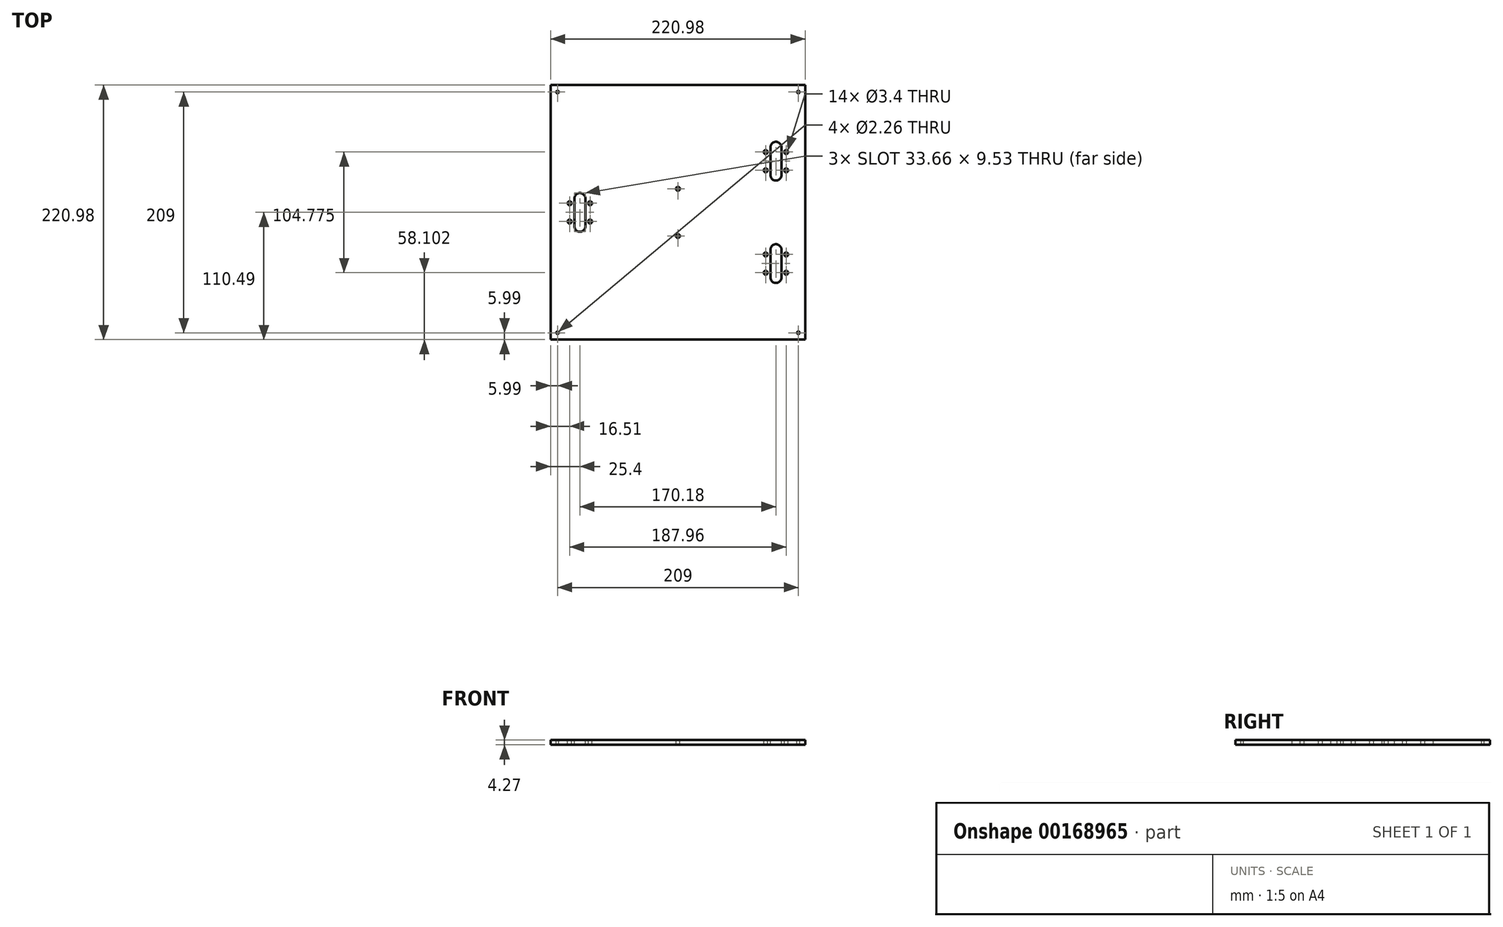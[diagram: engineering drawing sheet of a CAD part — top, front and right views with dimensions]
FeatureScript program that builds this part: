
annotation { "Feature Type Name" : "Feature", "Feature Type Description" : "" }
export const myFeature = defineFeature(function(context is Context, id is Id, definition is map)
    precondition{}
    {
        {
            var Q0;
            Q0=qCreatedBy(makeId("Top.planeOp"),FACE);
            var sketch = newSketch(context, id + "F0", { "sketchPlane" : qUnion([Q0])});
            skLineSegment(sketch, "E0.bottom", {"start": v(0, 0) * mm, "end": v(220.98, 0) * mm});
            skLineSegment(sketch, "E0.top", {"start": v(0, 220.98) * mm, "end": v(220.98, 220.98) * mm});
            skLineSegment(sketch, "E0.left", {"start": v(0, 0) * mm, "end": v(0, 220.98) * mm});
            skLineSegment(sketch, "E0.right", {"start": v(220.98, 0) * mm, "end": v(220.98, 220.98) * mm});
            skSolve(sketch);
        }
        {
            var Q0;
            Q0=makeQuery(id+"F0.imprint","IMPRINT",FACE,{"disambiguationData":[TD([[makeQuery(id+"F0.imprint","IMPRINT",EDGE,{"derivedFrom":sQuery(id+"F0.wireOp",EDGE,"E0.bottom")}),1.0]])]});
            extrude(context, id + "F1", {"entities" : qUnion([Q0]), "depth" : 4.27 * mm});
        }
        {
            var Q0;
            Q0=makeQuery(id+"F1.opExtrude","CAP_FACE",FACE,{"disambiguationData":[OSD([sQuery(id+"F0.wireOp",EDGE,"E0.bottom"),sQuery(id+"F0.wireOp",EDGE,"E0.top"),sQuery(id+"F0.wireOp",EDGE,"E0.left"),sQuery(id+"F0.wireOp",EDGE,"E0.right")])],"isStart":false});
            var sketch = newSketch(context, id + "F2", { "sketchPlane" : qUnion([Q0])});
            skLineSegment(sketch, "E1", {"start": v(110.5, 0) * mm, "end": v(110.5, 220.98) * mm});
            skLineSegment(sketch, "E2", {"start": v(0, 110.5) * mm, "end": v(220.98, 110.5) * mm});
            skPoint(sketch, "E3", {"position": v(6, 215) * mm});
            skPoint(sketch, "E4.MirrorP", {"position": v(214.99, 215) * mm});
            skPoint(sketch, "E5.MirrorP", {"position": v(215, 6) * mm});
            skPoint(sketch, "E6.MirrorP", {"position": v(6, 6) * mm});
            skSolve(sketch);
        }
        {
            var Q0;
            Q0=sQuery(id+"F2.wireOp",VERTEX,"E3");
            var Q1;
            Q1=sQuery(id+"F2.wireOp",VERTEX,"E4.MirrorP");
            var Q2;
            Q2=sQuery(id+"F2.wireOp",VERTEX,"E5.MirrorP");
            var Q3;
            Q3=sQuery(id+"F2.wireOp",VERTEX,"E6.MirrorP");
            var Q4;
            Q4=makeQuery(id+"F1.opExtrude","SWEPT_BODY",BODY,{"disambiguationData":[OSD([sQuery(id+"F0.wireOp",EDGE,"E0.bottom"),sQuery(id+"F0.wireOp",EDGE,"E0.top"),sQuery(id+"F0.wireOp",EDGE,"E0.left"),sQuery(id+"F0.wireOp",EDGE,"E0.right")])]});
            hole(context, id + "F3", {"style" : HoleStyle.SIMPLE, "endStyle" : HoleEndStyle.THROUGH, "standardTappedOrClearance" : lookupTablePath({ "standard" : "ANSI", "engagement" : "75%", "pitch" : "40 tpi", "size" : "#4", "type" : "Tapped" }), "standardBlindInLast" : lookupTablePath({ "standard" : "ANSI", "engagement" : "75%", "pitch" : "40 tpi", "size" : "#4", "type" : "Tapped" }), "holeDiameter" : 2.26 * mm, "locations" : qUnion([Q0, Q1, Q2, Q3]), "scope" : qUnion([Q4]), "isTappedThrough" : true, "majorDiameter" : 2.84 * mm, "showTappedDepth" : true});
        }
        {
            var Q0;
            Q0=makeQuery(id+"F1.opExtrude","CAP_FACE",FACE,{"disambiguationData":[OSD([sQuery(id+"F0.wireOp",EDGE,"E0.bottom"),sQuery(id+"F0.wireOp",EDGE,"E0.top"),sQuery(id+"F0.wireOp",EDGE,"E0.left"),sQuery(id+"F0.wireOp",EDGE,"E0.right")])],"isStart":false});
            var sketch = newSketch(context, id + "F4", { "sketchPlane" : qUnion([Q0])});
            skLineSegment(sketch, "E7", {"start": v(110.5, 220.98) * mm, "end": v(110.5, 0) * mm, "construction": true});
            skLineSegment(sketch, "E8", {"start": v(25.4, 220.98) * mm, "end": v(25.4, 0) * mm, "construction": true});
            skLineSegment(sketch, "E9.MirrorCS", {"start": v(195.58, 220.98) * mm, "end": v(195.58, 0) * mm, "construction": true});
            skLineSegment(sketch, "E10", {"start": v(0, 110.5) * mm, "end": v(220.98, 110.5) * mm, "construction": true});
            skLineSegment(sketch, "E11.left", {"start": v(20.64, 122.55) * mm, "end": v(20.64, 98.42) * mm});
            skLineSegment(sketch, "E11.right", {"start": v(30.16, 122.55) * mm, "end": v(30.16, 98.42) * mm});
            skArc(sketch, "E12", {"start": v(20.64, 122.55) * mm, "mid": v(25.4, 127.32) * mm, "end": v(30.16, 122.55) * mm});
            skArc(sketch, "E13.MirrorCS", {"start": v(20.64, 98.42) * mm, "mid": v(25.4, 93.66) * mm, "end": v(30.16, 98.42) * mm});
            skLineSegment(sketch, "E14.left", {"start": v(190.82, 78.1) * mm, "end": v(190.82, 53.98) * mm});
            skLineSegment(sketch, "E14.right", {"start": v(200.34, 78.1) * mm, "end": v(200.34, 53.98) * mm});
            skPoint(sketch, "E14.middle", {"position": v(195.58, 66.04) * mm});
            skArc(sketch, "E15", {"start": v(190.82, 78.1) * mm, "mid": v(195.58, 82.87) * mm, "end": v(200.34, 78.1) * mm});
            skArc(sketch, "E16", {"start": v(200.34, 53.98) * mm, "mid": v(195.58, 49.21) * mm, "end": v(190.82, 53.98) * mm});
            skArc(sketch, "E17.MirrorCS", {"start": v(200.34, 167) * mm, "mid": v(195.58, 171.77) * mm, "end": v(190.82, 167) * mm});
            skLineSegment(sketch, "E18.MirrorCS", {"start": v(190.82, 142.88) * mm, "end": v(190.82, 167) * mm});
            skArc(sketch, "E19.MirrorCS", {"start": v(190.82, 142.88) * mm, "mid": v(195.58, 138.11) * mm, "end": v(200.34, 142.88) * mm});
            skPoint(sketch, "E20.MirrorP", {"position": v(195.58, 154.94) * mm});
            skLineSegment(sketch, "E21.MirrorCS", {"start": v(200.34, 142.88) * mm, "end": v(200.34, 167) * mm});
            skSolve(sketch);
        }
        {
            var Q0;
            Q0 = qSketchRegion(id + "F4", true);
            extrude(context, id + "F5", {"entities" : qUnion([Q0]), "operationType" : NewBodyOperationType.REMOVE, "endBound" : BoundingType.THROUGH_ALL, "oppositeDirection" : true, "depth" : 25.4 * mm});
        }
        {
            var Q0;
            Q0=makeQuery(id+"F1.opExtrude","CAP_FACE",FACE,{"disambiguationData":[OSD([sQuery(id+"F0.wireOp",EDGE,"E0.bottom"),sQuery(id+"F0.wireOp",EDGE,"E0.top"),sQuery(id+"F0.wireOp",EDGE,"E0.left"),sQuery(id+"F0.wireOp",EDGE,"E0.right")])],"isStart":false});
            var sketch = newSketch(context, id + "F6", { "sketchPlane" : qUnion([Q0])});
            skLineSegment(sketch, "E22", {"start": v(110.5, 220.98) * mm, "end": v(110.5, 0) * mm});
            skLineSegment(sketch, "E23", {"start": v(110.5, 110.5) * mm, "end": v(220.98, 110.5) * mm});
            skPoint(sketch, "E24", {"position": v(110.5, 131) * mm});
            skPoint(sketch, "E25", {"position": v(110.5, 90) * mm});
            skSolve(sketch);
        }
        {
            var Q0;
            Q0=sQuery(id+"F6.wireOp",VERTEX,"E24");
            var Q1;
            Q1=sQuery(id+"F6.wireOp",VERTEX,"E25");
            var Q2;
            Q2=makeQuery(id+"F1.opExtrude","SWEPT_BODY",BODY,{"disambiguationData":[OSD([sQuery(id+"F0.wireOp",EDGE,"E0.bottom"),sQuery(id+"F0.wireOp",EDGE,"E0.top"),sQuery(id+"F0.wireOp",EDGE,"E0.left"),sQuery(id+"F0.wireOp",EDGE,"E0.right")])]});
            hole(context, id + "F7", {"style" : HoleStyle.SIMPLE, "endStyle" : HoleEndStyle.THROUGH, "holeDiameter" : 3.4 * mm, "locations" : qUnion([Q0, Q1]), "scope" : qUnion([Q2]), "isTappedThrough" : true});
        }
        {
            var Q0;
            Q0=makeQuery(id+"F1.opExtrude","CAP_FACE",FACE,{"disambiguationData":[OSD([sQuery(id+"F0.wireOp",EDGE,"E0.bottom"),sQuery(id+"F0.wireOp",EDGE,"E0.top"),sQuery(id+"F0.wireOp",EDGE,"E0.left"),sQuery(id+"F0.wireOp",EDGE,"E0.right")])],"isStart":false});
            var sketch = newSketch(context, id + "F8", { "sketchPlane" : qUnion([Q0])});
            skLineSegment(sketch, "E26", {"start": v(25.4, 122.55) * mm, "end": v(25.4, 98.42) * mm, "construction": true});
            skLineSegment(sketch, "E27", {"start": v(25.4, 110.49) * mm, "end": v(0, 110.5) * mm});
            skPoint(sketch, "E28", {"position": v(16.5, 118.43) * mm});
            skPoint(sketch, "E29", {"position": v(16.5, 102.55) * mm});
            skPoint(sketch, "E30.MirrorP", {"position": v(34.29, 118.43) * mm});
            skPoint(sketch, "E31.MirrorP", {"position": v(34.3, 102.55) * mm});
            skLineSegment(sketch, "E32", {"start": v(195.58, 167) * mm, "end": v(195.58, 142.88) * mm});
            skLineSegment(sketch, "E33", {"start": v(195.58, 154.94) * mm, "end": v(220.98, 154.94) * mm});
            skPoint(sketch, "E34", {"position": v(204.47, 162.88) * mm});
            skPoint(sketch, "E35", {"position": v(204.47, 147) * mm});
            skPoint(sketch, "E36.MirrorP", {"position": v(186.69, 162.88) * mm});
            skPoint(sketch, "E37.MirrorP", {"position": v(186.69, 147) * mm});
            skPoint(sketch, "E38.MirrorP", {"position": v(204.47, 73.98) * mm});
            skPoint(sketch, "E39.MirrorP", {"position": v(204.47, 58.1) * mm});
            skPoint(sketch, "E40.MirrorP", {"position": v(186.69, 58.1) * mm});
            skPoint(sketch, "E41.MirrorP", {"position": v(186.69, 73.98) * mm});
            skSolve(sketch);
        }
        {
            var Q0;
            Q0=sQuery(id+"F8.wireOp",VERTEX,"E28");
            var Q1;
            Q1=sQuery(id+"F8.wireOp",VERTEX,"E29");
            var Q2;
            Q2=sQuery(id+"F8.wireOp",VERTEX,"E30.MirrorP");
            var Q3;
            Q3=sQuery(id+"F8.wireOp",VERTEX,"E31.MirrorP");
            var Q4;
            Q4=sQuery(id+"F8.wireOp",VERTEX,"E34");
            var Q5;
            Q5=sQuery(id+"F8.wireOp",VERTEX,"E37.MirrorP");
            var Q6;
            Q6=sQuery(id+"F8.wireOp",VERTEX,"E36.MirrorP");
            var Q7;
            Q7=sQuery(id+"F8.wireOp",VERTEX,"E35");
            var Q8;
            Q8=sQuery(id+"F8.wireOp",VERTEX,"E38.MirrorP");
            var Q9;
            Q9=sQuery(id+"F8.wireOp",VERTEX,"E40.MirrorP");
            var Q10;
            Q10=sQuery(id+"F8.wireOp",VERTEX,"E39.MirrorP");
            var Q11;
            Q11=sQuery(id+"F8.wireOp",VERTEX,"E41.MirrorP");
            var Q12;
            Q12=makeQuery(id+"F1.opExtrude","SWEPT_BODY",BODY,{"disambiguationData":[OSD([sQuery(id+"F0.wireOp",EDGE,"E0.bottom"),sQuery(id+"F0.wireOp",EDGE,"E0.top"),sQuery(id+"F0.wireOp",EDGE,"E0.left"),sQuery(id+"F0.wireOp",EDGE,"E0.right")])]});
            hole(context, id + "F9", {"style" : HoleStyle.SIMPLE, "endStyle" : HoleEndStyle.THROUGH, "holeDiameter" : 3.4 * mm, "locations" : qUnion([Q0, Q1, Q2, Q3, Q4, Q5, Q6, Q7, Q8, Q9, Q10, Q11]), "scope" : qUnion([Q12]), "isTappedThrough" : true});
        }
    });
